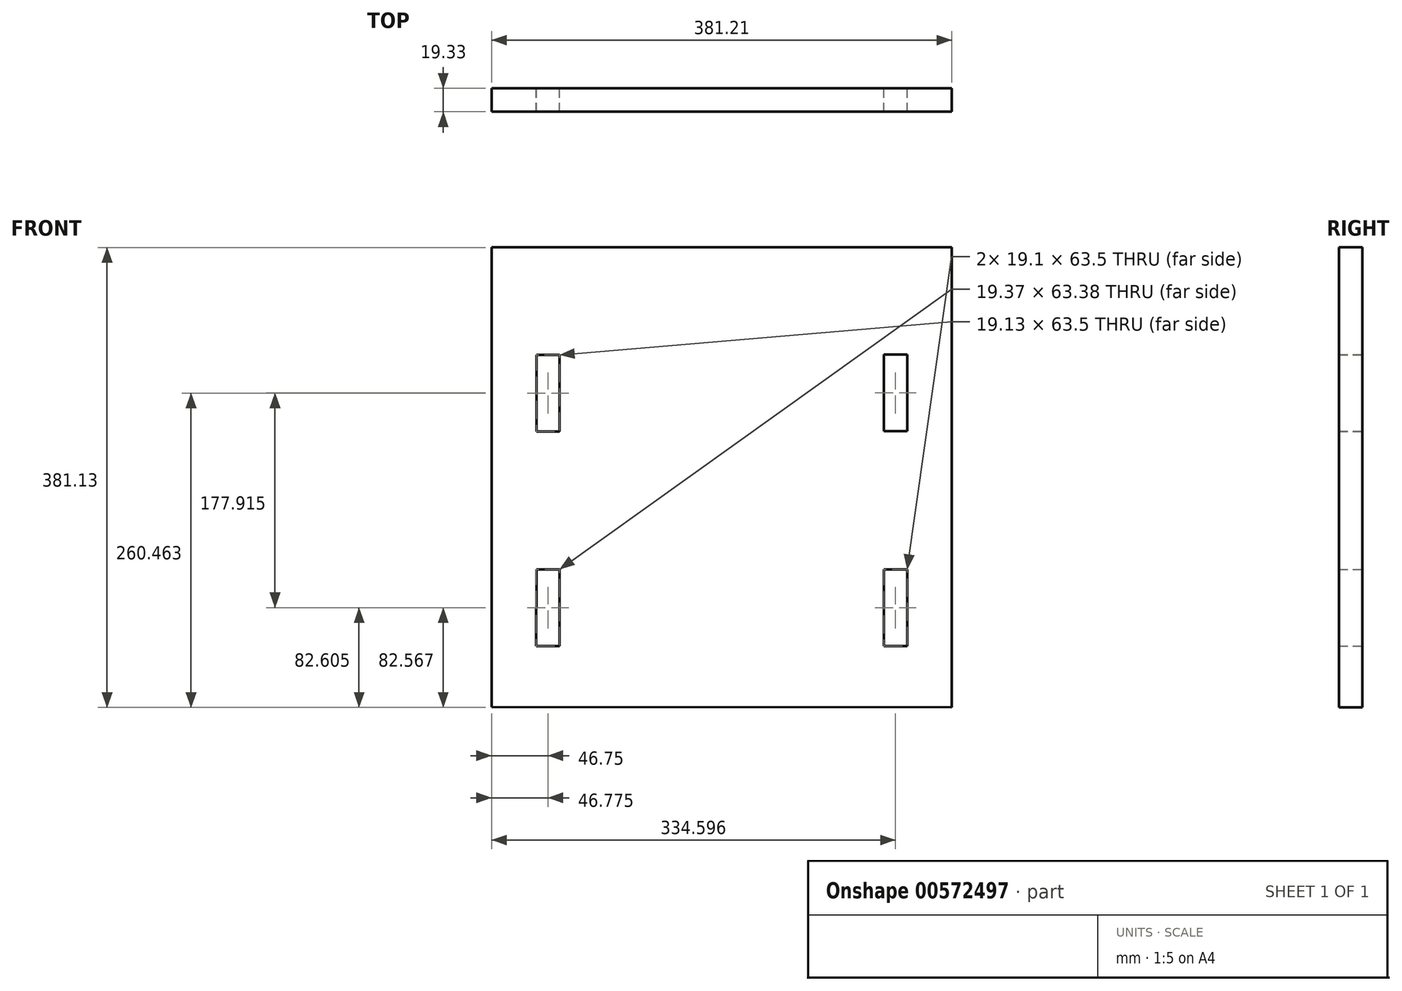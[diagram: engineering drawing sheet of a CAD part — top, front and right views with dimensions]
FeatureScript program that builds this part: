
annotation { "Feature Type Name" : "Feature", "Feature Type Description" : "" }
export const myFeature = defineFeature(function(context is Context, id is Id, definition is map)
    precondition{}
    {
        {
            var Q0;
            Q0=qCreatedBy(makeId("Front.planeOp"),FACE);
            var sketch = newSketch(context, id + "F0", { "sketchPlane" : qUnion([Q0])});
            skLineSegment(sketch, "E0.bottom", {"start": v(-117.93, 395.92) * mm, "end": v(263.07, 395.92) * mm});
            skLineSegment(sketch, "E1.bottom", {"start": v(226, 307.02) * mm, "end": v(206.9, 307.02) * mm});
            skLineSegment(sketch, "E1.top", {"start": v(226, 243.52) * mm, "end": v(206.9, 243.52) * mm});
            skLineSegment(sketch, "E1.left", {"start": v(226, 307.02) * mm, "end": v(226, 243.52) * mm});
            skLineSegment(sketch, "E1.right", {"start": v(206.9, 307.02) * mm, "end": v(206.9, 243.52) * mm});
            skLineSegment(sketch, "E2.bottom", {"start": v(206.9, 129.1) * mm, "end": v(226, 129.1) * mm});
            skLineSegment(sketch, "E2.top", {"start": v(206.9, 65.6) * mm, "end": v(226, 65.6) * mm});
            skLineSegment(sketch, "E2.left", {"start": v(206.9, 129.1) * mm, "end": v(206.9, 65.6) * mm});
            skLineSegment(sketch, "E2.right", {"start": v(226, 129.1) * mm, "end": v(226, 65.6) * mm});
            skLineSegment(sketch, "E3.MirrorCS", {"start": v(-80.92, 307) * mm, "end": v(-61.82, 307) * mm});
            skLineSegment(sketch, "E4.MirrorCS", {"start": v(-80.96, 243.5) * mm, "end": v(-61.92, 243.5) * mm});
            skLineSegment(sketch, "E5.MirrorCS", {"start": v(-61.91, 129.09) * mm, "end": v(-61.68, 65.7) * mm});
            skLineSegment(sketch, "E6.MirrorCS", {"start": v(-81.02, 129.09) * mm, "end": v(-81.05, 65.7) * mm});
            skLineSegment(sketch, "E7.MirrorCS", {"start": v(-61.91, 129.09) * mm, "end": v(-81.02, 129.09) * mm});
            skLineSegment(sketch, "E8.MirrorCS", {"start": v(-61.68, 65.7) * mm, "end": v(-81.05, 65.7) * mm});
            skLineSegment(sketch, "E9.MirrorCS", {"start": v(-80.92, 307) * mm, "end": v(-80.96, 243.5) * mm});
            skLineSegment(sketch, "E10.MirrorCS", {"start": v(-61.82, 307) * mm, "end": v(-61.92, 243.5) * mm});
            skLineSegment(sketch, "E11", {"start": v(-118.14, 14.92) * mm, "end": v(263.07, 14.79) * mm});
            skLineSegment(sketch, "E12", {"start": v(-117.93, 395.92) * mm, "end": v(-118.14, 14.92) * mm});
            skLineSegment(sketch, "E13", {"start": v(263.07, 395.92) * mm, "end": v(263.07, 14.79) * mm});
            skSolve(sketch);
        }
        {
            var Q0;
            Q0 = qSketchRegion(id + "F0", true);
            extrude(context, id + "F1", {"entities" : qUnion([Q0]), "depth" : 19.33 * mm, "offsetDistance" : 25.4 * mm});
        }
    });
